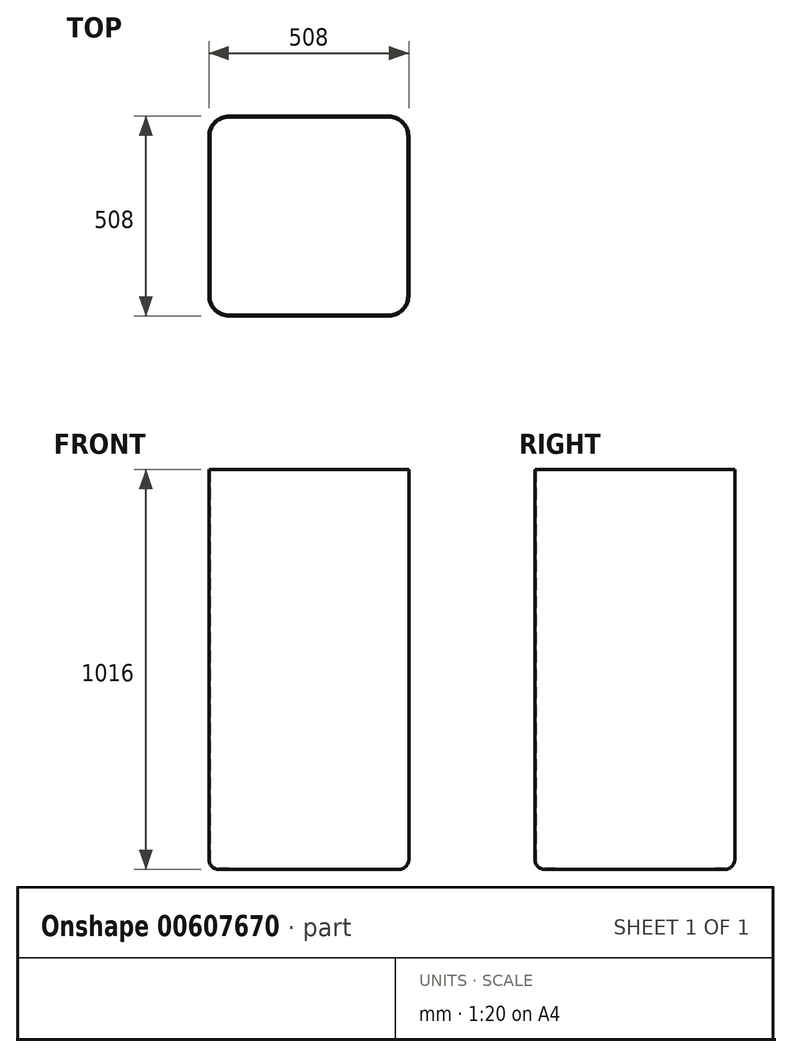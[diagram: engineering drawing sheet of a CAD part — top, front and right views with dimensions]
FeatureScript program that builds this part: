
annotation { "Feature Type Name" : "Feature", "Feature Type Description" : "" }
export const myFeature = defineFeature(function(context is Context, id is Id, definition is map)
    precondition{}
    {
        {
            var Q0;
            Q0=qCreatedBy(makeId("Top.planeOp"),FACE);
            var sketch = newSketch(context, id + "F0", { "sketchPlane" : qUnion([Q0])});
            skLineSegment(sketch, "E0", {"start": v(0, 0) * mm, "end": v(254, 0) * mm});
            skLineSegment(sketch, "E1", {"start": v(254, 0) * mm, "end": v(254, 254) * mm});
            skLineSegment(sketch, "E2.bottom", {"start": v(254, 254) * mm, "end": v(-254, 254) * mm});
            skLineSegment(sketch, "E2.top", {"start": v(254, -254) * mm, "end": v(-254, -254) * mm});
            skLineSegment(sketch, "E2.left", {"start": v(254, 254) * mm, "end": v(254, -254) * mm});
            skLineSegment(sketch, "E2.right", {"start": v(-254, 254) * mm, "end": v(-254, -254) * mm});
            skPoint(sketch, "E2.middle", {"position": v(0, 0) * mm});
            skSolve(sketch);
        }
        {
            var Q0;
            Q0 = qSketchRegion(id + "F0", true);
            extrude(context, id + "F1", {"entities" : qUnion([Q0]), "depth" : 1016 * mm, "offsetDistance" : 25.4 * mm});
        }
        {
            var Q0;
            Q0=makeQuery(id+"F1.opExtrude","CAP_EDGE",EDGE,{"disambiguationData":[OSD([sQuery(id+"F0.wireOp",EDGE,"E2.right")])],"isStart":true});
            var Q1;
            Q1=makeQuery(id+"F1.opExtrude","CAP_EDGE",EDGE,{"disambiguationData":[OSD([sQuery(id+"F0.wireOp",EDGE,"E2.bottom")])],"isStart":true});
            var Q2;
            Q2=makeQuery(id+"F1.opExtrude","CAP_EDGE",EDGE,{"disambiguationData":[OSD([sQuery(id+"F0.wireOp",EDGE,"E2.top")])],"isStart":true});
            var Q3;
            Q3=makeQuery(id+"F1.opExtrude","CAP_EDGE",EDGE,{"disambiguationData":[OSD([sQuery(id+"F0.wireOp",EDGE,"E2.left")])],"isStart":true});
            fillet(context, id + "F2", {"entities" : qUnion([Q0, Q1, Q2, Q3]), "radius" : 25.4 * mm, "tangentPropagation" : true, "allowEdgeOverflow" : false});
        }
        {
            var Q0;
            Q0=makeQuery(id+"F1.opExtrude","SWEPT_EDGE",EDGE,{"disambiguationData":[OSD([sQuery(id+"F0.wireOp",EDGE,"E2.bottom"),sQuery(id+"F0.wireOp",EDGE,"E2.right")])]});
            var Q1;
            Q1=makeQuery(id+"F1.opExtrude","SWEPT_EDGE",EDGE,{"disambiguationData":[OSD([sQuery(id+"F0.wireOp",EDGE,"E2.top"),sQuery(id+"F0.wireOp",EDGE,"E2.right")])]});
            var Q2;
            Q2=makeQuery(id+"F1.opExtrude","SWEPT_EDGE",EDGE,{"disambiguationData":[OSD([sQuery(id+"F0.wireOp",EDGE,"E2.bottom"),sQuery(id+"F0.wireOp",EDGE,"E2.left")])]});
            var Q3;
            Q3=makeQuery(id+"F1.opExtrude","SWEPT_EDGE",EDGE,{"disambiguationData":[OSD([sQuery(id+"F0.wireOp",EDGE,"E2.top"),sQuery(id+"F0.wireOp",EDGE,"E2.left")])]});
            fillet(context, id + "F3", {"entities" : qUnion([Q0, Q1, Q2, Q3]), "radius" : 50.8 * mm, "tangentPropagation" : true, "allowEdgeOverflow" : false});
        }
        {
            var Q0;
            Q0=makeQuery(id+"F1.opExtrude","CAP_FACE",FACE,{"disambiguationData":[OSD([sQuery(id+"F0.wireOp",EDGE,"E2.bottom"),sQuery(id+"F0.wireOp",EDGE,"E2.top"),sQuery(id+"F0.wireOp",EDGE,"E2.left"),sQuery(id+"F0.wireOp",EDGE,"E2.right")])],"isStart":false});
            shell(context, id + "F4", {"entities" : qUnion([Q0]), "thickness" : 2.54 * mm});
        }
    });
